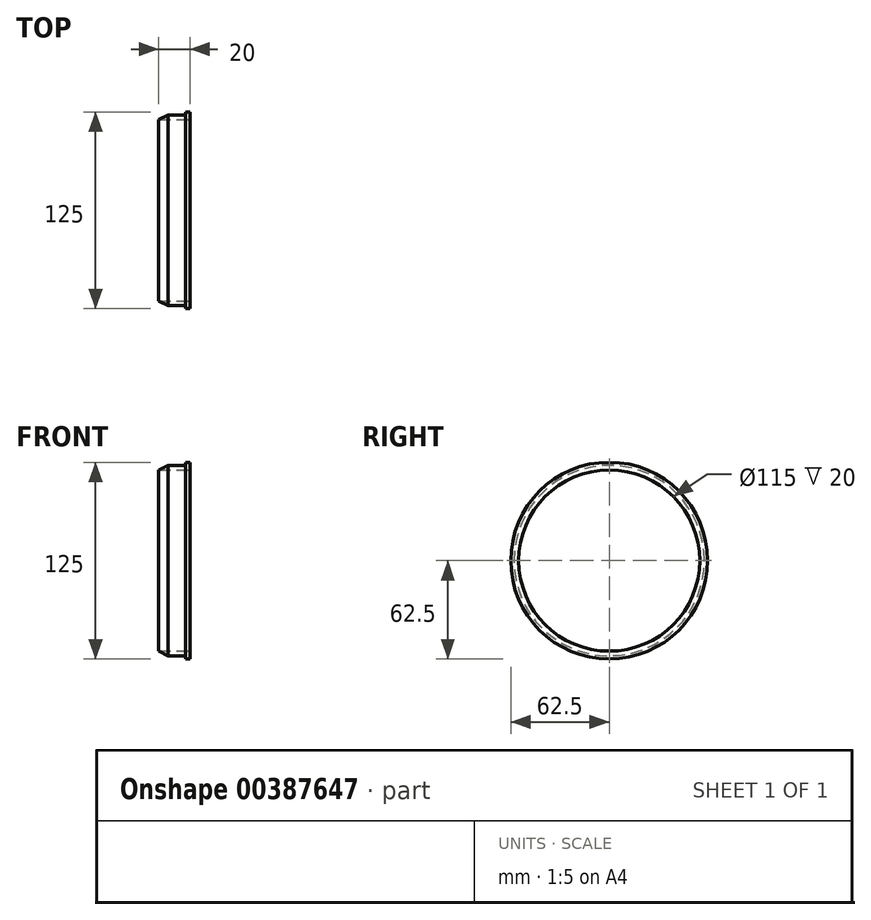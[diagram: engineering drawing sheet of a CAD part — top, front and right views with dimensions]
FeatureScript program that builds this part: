
annotation { "Feature Type Name" : "Feature", "Feature Type Description" : "" }
export const myFeature = defineFeature(function(context is Context, id is Id, definition is map)
    precondition{}
    {
        {
            var Q0;
            Q0=qCreatedBy(makeId("Right.planeOp"),FACE);
            var sketch = newSketch(context, id + "F0", { "sketchPlane" : qUnion([Q0])});
            skCircle(sketch, "E0", {"center": v(0, 0) * mm, "radius": 57.5 * mm});
            skPoint(sketch, "E1", {"position": v(0, 57.5) * mm});
            skSolve(sketch);
        }
        {
            var Q0;
            Q0=qCreatedBy(makeId("Front.planeOp"),FACE);
            var sketch = newSketch(context, id + "F1", { "sketchPlane" : qUnion([Q0])});
            skLineSegment(sketch, "E2", {"start": v(0, 57.5) * mm, "end": v(20, 57.5) * mm});
            skLineSegment(sketch, "E3", {"start": v(20, 57.5) * mm, "end": v(20, 62.5) * mm});
            skLineSegment(sketch, "E4", {"start": v(20, 62.5) * mm, "end": v(17, 62.5) * mm});
            skLineSegment(sketch, "E5", {"start": v(17, 62.5) * mm, "end": v(17, 60.5) * mm});
            skLineSegment(sketch, "E6", {"start": v(17, 60.5) * mm, "end": v(6, 60.5) * mm});
            skLineSegment(sketch, "E7", {"start": v(6, 60.5) * mm, "end": v(0, 57.5) * mm});
            skSolve(sketch);
        }
        {
            var Q0;
            Q0=makeQuery(id+"F1.imprint","IMPRINT",FACE,{"disambiguationData":[TD([[makeQuery(id+"F1.imprint","IMPRINT",EDGE,{"derivedFrom":sQuery(id+"F1.wireOp",EDGE,"E2")}),1.0]])]});
            var Q1;
            Q1=sQuery(id+"F0.wireOp",EDGE,"E0");
            sweep(context, id + "F2", {"profiles" : qUnion([Q0]), "path" : qUnion([Q1])});
        }
    });
